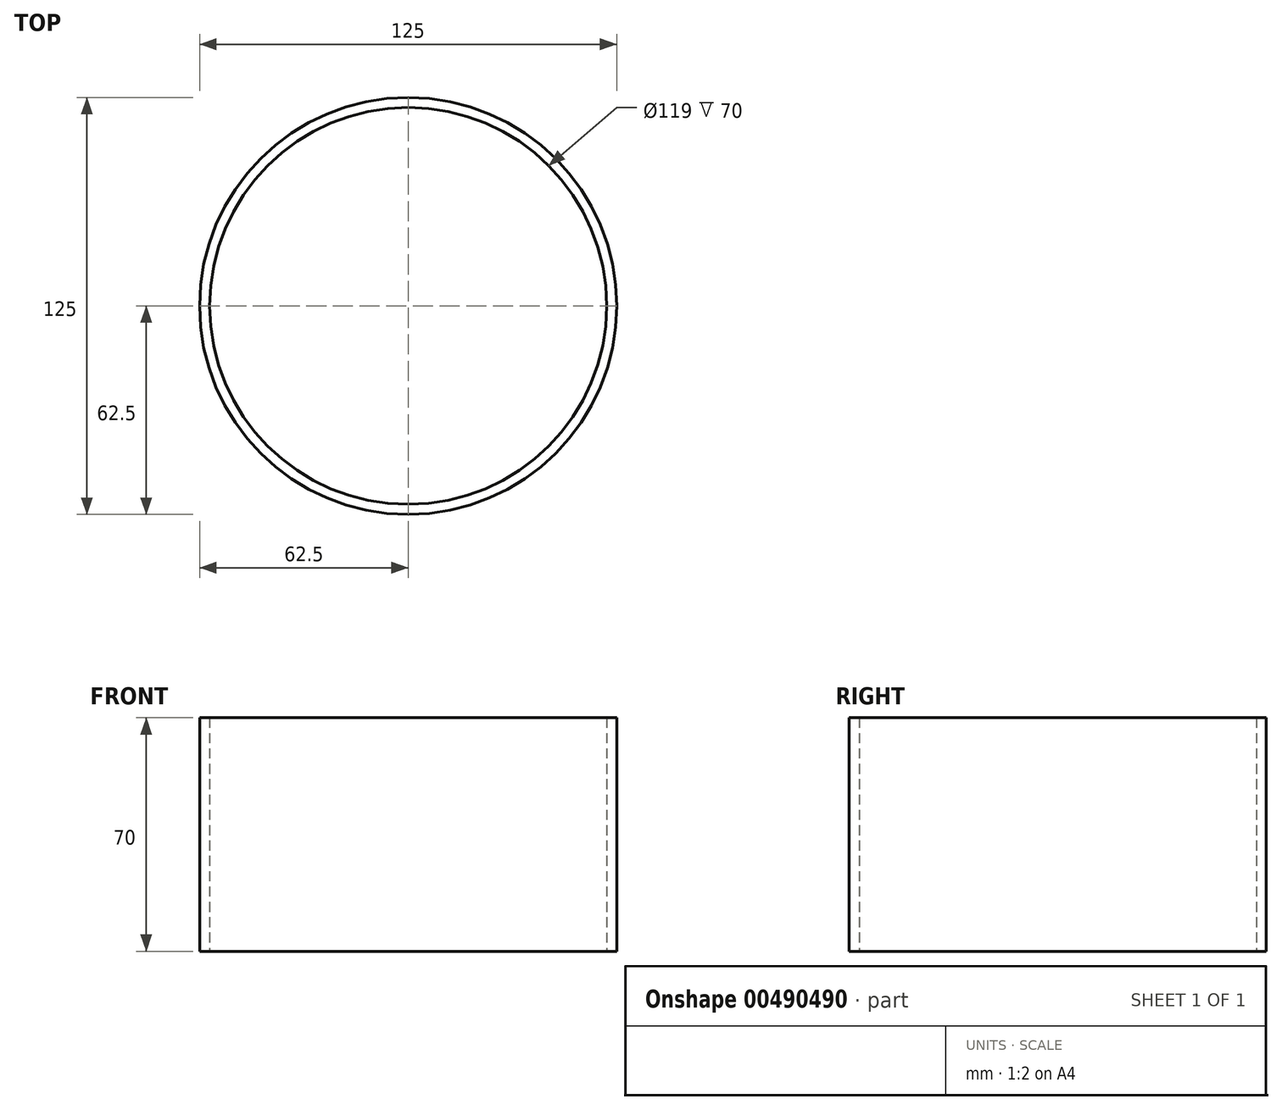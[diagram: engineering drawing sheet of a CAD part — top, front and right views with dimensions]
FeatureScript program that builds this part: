
annotation { "Feature Type Name" : "Feature", "Feature Type Description" : "" }
export const myFeature = defineFeature(function(context is Context, id is Id, definition is map)
    precondition{}
    {
        {
            var Q0;
            Q0=qCreatedBy(makeId("Top.planeOp"),FACE);
            var sketch = newSketch(context, id + "F0", { "sketchPlane" : qUnion([Q0])});
            skCircle(sketch, "E0", {"center": v(0, 0) * mm, "radius": 59.5 * mm});
            skCircle(sketch, "E1", {"center": v(0, 0) * mm, "radius": 62.5 * mm});
            skSolve(sketch);
        }
        {
            var Q0;
            Q0=makeQuery(id+"F0.imprint","IMPRINT",FACE,{"disambiguationData":[TD([[makeQuery(id+"F0.imprint","IMPRINT",EDGE,{"derivedFrom":sQuery(id+"F0.wireOp",EDGE,"E0")}),-1.0]])]});
            extrude(context, id + "F1", {"entities" : qUnion([Q0]), "depth" : 70 * mm});
        }
    });
